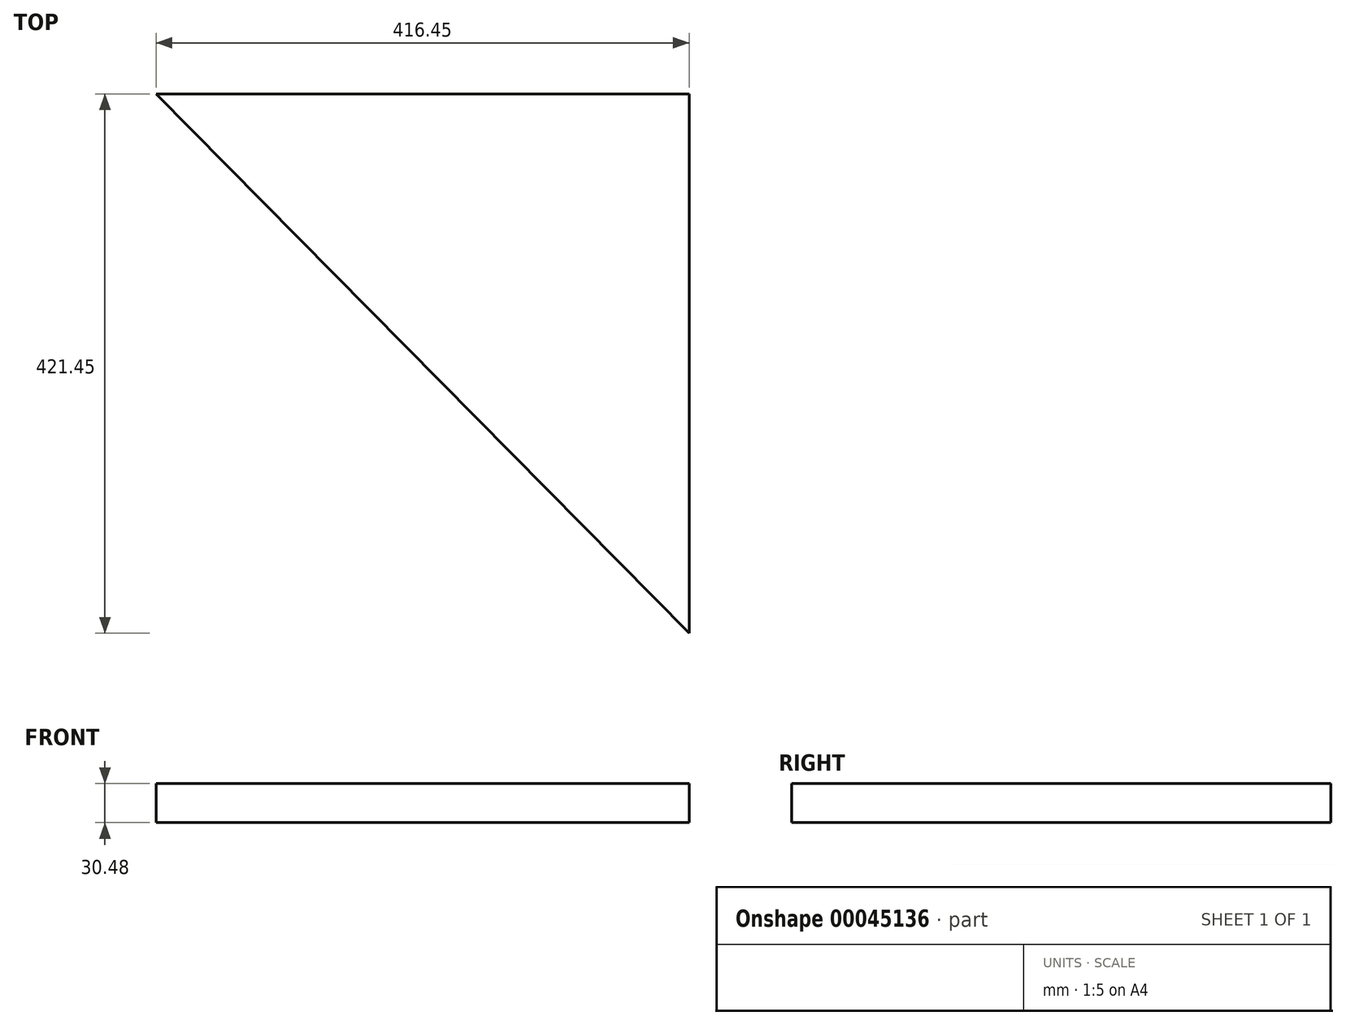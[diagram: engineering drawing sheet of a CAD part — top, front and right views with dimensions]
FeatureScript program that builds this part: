
annotation { "Feature Type Name" : "Feature", "Feature Type Description" : "" }
export const myFeature = defineFeature(function(context is Context, id is Id, definition is map)
    precondition{}
    {
        {
            var Q0;
            Q0=qCreatedBy(makeId("Top.planeOp"),FACE);
            var sketch = newSketch(context, id + "F0", { "sketchPlane" : qUnion([Q0])});
            skLineSegment(sketch, "E0", {"start": v(-198.82, 189.32) * mm, "end": v(217.63, -232.13) * mm});
            skLineSegment(sketch, "E1", {"start": v(217.63, -232.13) * mm, "end": v(217.63, 189.32) * mm});
            skLineSegment(sketch, "E2", {"start": v(217.63, 189.32) * mm, "end": v(-198.82, 189.32) * mm});
            skLineSegment(sketch, "E3", {"start": v(217.63, -232.13) * mm, "end": v(217.63, -21.4) * mm});
            skSolve(sketch);
        }
        {
            var Q0;
            Q0=makeQuery(id+"F0.imprint","IMPRINT",FACE,{"disambiguationData":[TD([[makeQuery(id+"F0.imprint","IMPRINT",EDGE,{"derivedFrom":sQuery(id+"F0.wireOp",EDGE,"E0")}),1.0]])]});
            extrude(context, id + "F1", {"entities" : qUnion([Q0]), "depth" : 30.48 * mm});
        }
    });
